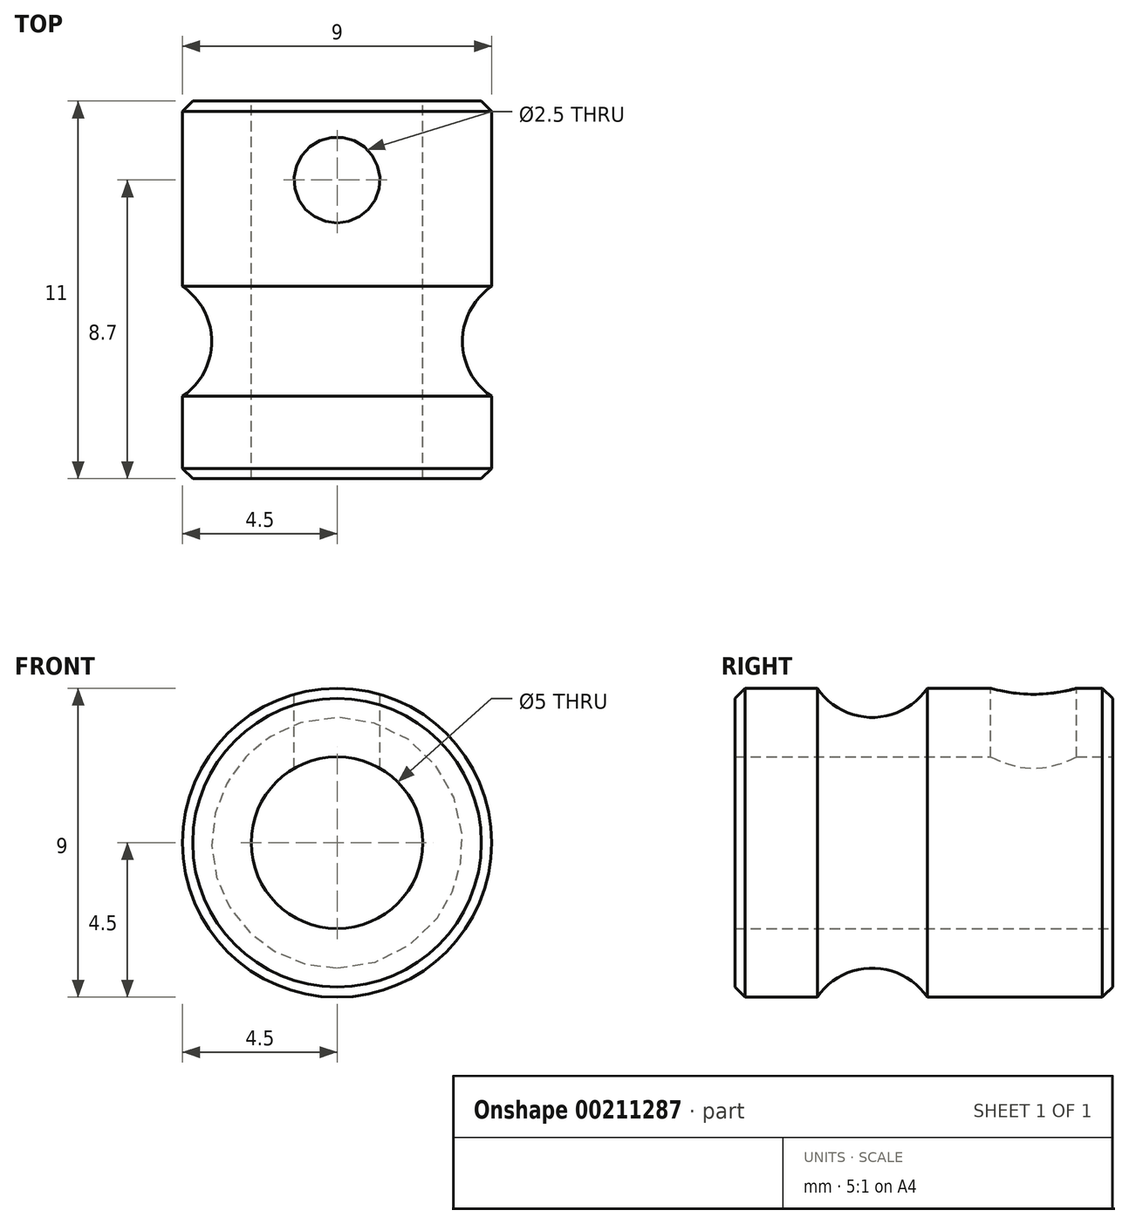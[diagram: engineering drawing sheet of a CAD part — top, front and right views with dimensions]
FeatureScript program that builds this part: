
annotation { "Feature Type Name" : "Feature", "Feature Type Description" : "" }
export const myFeature = defineFeature(function(context is Context, id is Id, definition is map)
    precondition{}
    {
        {
            var Q0;
            Q0=qCreatedBy(makeId("Front.planeOp"),FACE);
            var sketch = newSketch(context, id + "F0", { "sketchPlane" : qUnion([Q0])});
            skCircle(sketch, "E0", {"center": v(0, 0) * mm, "radius": 2.5 * mm});
            skCircle(sketch, "E1", {"center": v(0, 0) * mm, "radius": 4.5 * mm});
            skSolve(sketch);
        }
        {
            var Q0;
            Q0=makeQuery(id+"F0.imprint","IMPRINT",FACE,{"disambiguationData":[TD([[makeQuery(id+"F0.imprint","IMPRINT",EDGE,{"derivedFrom":sQuery(id+"F0.wireOp",EDGE,"E0")}),-1.0]])]});
            extrude(context, id + "F1", {"entities" : qUnion([Q0]), "endBound" : BoundingType.SYMMETRIC, "depth" : 11 * mm});
        }
        {
            var Q0;
            Q0=qCreatedBy(makeId("Right.planeOp"),FACE);
            var sketch = newSketch(context, id + "F2", { "sketchPlane" : qUnion([Q0])});
            skLineSegment(sketch, "E2", {"start": v(5.5, 0) * mm, "end": v(-5.5, 0) * mm, "construction": true});
            skLineSegment(sketch, "E3", {"start": v(-1.5, 0) * mm, "end": v(-1.5, 3.65) * mm, "construction": true});
            skLineSegment(sketch, "E4", {"start": v(3.2, 0) * mm, "end": v(3.2, 4.5) * mm});
            skCircle(sketch, "E5", {"center": v(-1.5, 5.58) * mm, "radius": 1.93 * mm});
            skLineSegment(sketch, "E6", {"start": v(-1.5, 5.58) * mm, "end": v(-1.5, 3.65) * mm, "construction": true});
            skLineSegment(sketch, "E7", {"start": v(-3.1, 4.5) * mm, "end": v(0.1, 4.5) * mm, "construction": true});
            skSolve(sketch);
        }
        {
            var Q0;
            Q0=makeQuery(id+"F2.imprint","IMPRINT",FACE,{"disambiguationData":[TD([[makeQuery(id+"F2.imprint","IMPRINT",EDGE,{"derivedFrom":sQuery(id+"F2.wireOp",EDGE,"E5")}),1.0]])]});
            var Q1;
            Q1=sQuery(id+"F2.wireOp",EDGE,"E2");
            revolve(context, id + "F3", {"operationType" : NewBodyOperationType.REMOVE, "entities" : qUnion([Q0]), "axis" : qUnion([Q1]), "revolveType" : RevolveType.FULL, "oppositeDirection" : true});
        }
        {
            var Q0;
            Q0=sQuery(id+"F2.wireOp",VERTEX,"E4.end");
            var Q1;
            Q1=sQuery(id+"F2.wireOp",EDGE,"E4");
            cPlane(context, id + "F4", {"entities" : qUnion([Q0, Q1]), "cplaneType" : CPlaneType.LINE_POINT, "offset" : 25 * mm, "width" : 150 * mm, "height" : 150 * mm});
        }
        {
            var Q0;
            Q0=qCreatedBy(id+"F4.planeOp",FACE);
            var sketch = newSketch(context, id + "F5", { "sketchPlane" : qUnion([Q0])});
            skPoint(sketch, "E8.0", {"position": v(0, 3.2) * mm});
            skSolve(sketch);
        }
        {
            var Q0;
            Q0=sQuery(id+"F5.wireOp",VERTEX,"E8.0");
            var Q1;
            Q1=makeQuery(id+"F1.opExtrude","SWEPT_BODY",BODY,{"disambiguationData":[OSD([sQuery(id+"F0.wireOp",EDGE,"E0"),sQuery(id+"F0.wireOp",EDGE,"E1")])]});
            hole(context, id + "F6", {"style" : HoleStyle.SIMPLE, "endStyle" : HoleEndStyle.BLIND, "holeDiameter" : 2.5 * mm, "holeDepth" : 4.5 * mm, "locations" : qUnion([Q0]), "scope" : qUnion([Q1])});
        }
        {
            var Q0;
            Q0=makeQuery(id+"F1.opExtrude","CAP_EDGE",EDGE,{"disambiguationData":[OSD([sQuery(id+"F0.wireOp",EDGE,"E1")])],"isStart":false});
            var Q1;
            Q1=makeQuery(id+"F1.opExtrude","CAP_EDGE",EDGE,{"disambiguationData":[OSD([sQuery(id+"F0.wireOp",EDGE,"E1")])],"isStart":true});
            chamfer(context, id + "F7", {"entities" : qUnion([Q0, Q1]), "width" : .3 * mm, "tangentPropagation" : true});
        }
    });
